# Revit family: svetilnik_alfresco_solyaris-3
name_source: partatom
category: Осветительные приборы
revit_build: Autodesk Revit 2016 (Build: 20150714_1515(x64)
units: mm (PartAtom-declared; Revit-internal decimal feet)

## family parameters
Всегда вертикально = Да
Источник света = Нет
На основе рабочей плоскости = Нет
Общий = Нет
При загрузке вырезать с полостями = Нет
Размер круглого соединителя = Использовать диаметр
Тип детали = Нормальный
Точка расчета площади = Нет

## types (4) — shared parameters
ADSK_Единица измерения = шт
ADSK_Классификация нагрузок = Освещение
ADSK_Количество фаз = 2
ADSK_Количество фаз числовое = 2
ADSK_Коэффициент мощности = 0.97
ADSK_Модель = Солярис 3-2
ADSK_Напряжение = 220 В
ADSK_Размер_Высота = 3900 мм
ADSK_Размер_Ширина = 700 мм
ADSK_Энергоэффективность = 90 лм/Вт
IP Class = IP 54
URL = http://www.allfresco.ru
Блок аварийного питания = Нет
Изготовитель = ALFRESCO
Класс Защиты = 1
Класс пожароопасности = F (светильники предназначены для установки непосредственно на поверхность из нормально воспламеняемых матеоиалов)
Климатическая зона = УХЛ1
Область использования = Ландшафт, коттедж.поселки,микрорайоны,АЗС, автостоянки
Температура эксплуатации = -35 +40
Тип ИС = МГЛ-лампа
Тип КСС = Sym
Тип ПРА = ЭМПРА
Тип продукции = Комплект(Опора освещения+ светильник)
Цветовая температура = 4000

## per-type parameters (varying)
| type | ADSK_Артикул | ADSK_Масса | ADSK_Наименование | ADSK_Номинальная мощность | ADSK_Полная мощность | ADSK_Размер_Длина | ADSK_Ток | Полная установленная мощность | Световой поток | Солярис 3-2 | Тип светильника |
| Солярис-3-2-10 ЧС и прожектор 70Вт | 1123000880 | 78 | Солярис-3-2 — опора освещения Солярис-3-2-10 ЧС и прожектор 70Вт | 140 Вт | 144 В·А | 2136 мм | 0 А | 144 В·А | 12600 лм | Да | Солярис3 : Солярис3-70Вт |
| Солярис-3-2-10 ЧС и прожектор 150Вт | 1123000890 | 80 | Солярис-3-2 — опора освещения Солярис-3-2-10 ЧС и прожектор 150Вт | 300 Вт | 309 В·А | 2136 мм | 1 А | 309 В·А | 27000 лм | Да | Солярис3 : Солярис3-150Вт |
| Солярис-3-1-10 ЧС и прожектор 70Вт | 1123000900 | 59 | Солярис-3-1 — опора освещения Солярис-3-1-10 ЧС и прожектор 70Вт | 70 Вт | 72 В·А | 1118 мм | 0 А | 72 В·А | 6300 лм | Нет | Солярис3 : Солярис3-70Вт |
| Солярис-3-1-10 ЧС и прожектор 150Вт | 1123000910 | 61 | Солярис-3-1 — опора освещения Солярис-3-1-10 ЧС и прожектор 70Вт | 150 Вт | 155 В·А | 1118 мм | 0 А | 155 В·А | 13500 лм | Нет | Солярис3 : Солярис3-150Вт |
